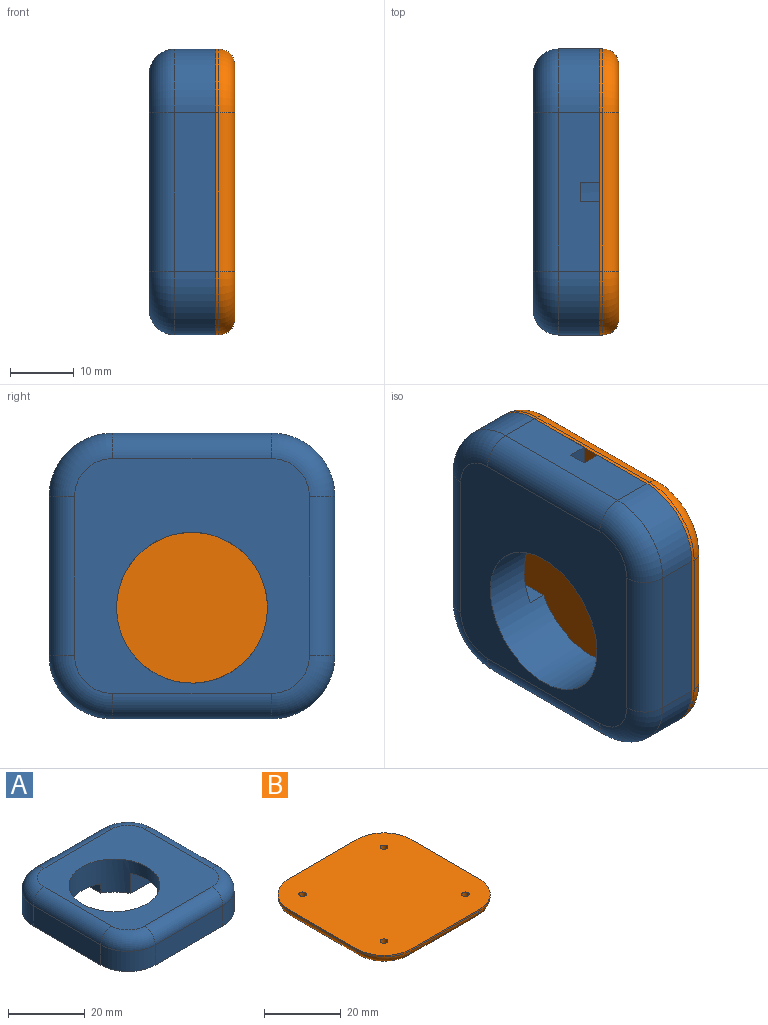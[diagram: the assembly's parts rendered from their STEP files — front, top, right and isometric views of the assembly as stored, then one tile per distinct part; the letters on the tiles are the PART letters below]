
ASSEMBLY  parts=2 mates=1
PART A: 42 faces, bbox 46.6x46.6x10.5 mm
  f0: plane 45x45mm, normal (0,0,-1), area 1167.3mm2, adj f1,f2,f3,f4,f6,f7,f8,f11
  f1: plane 25x6.5mm, normal (1,0,0), area 153.5mm2, adj f0,f7,f8,f9,f20,f21,f23
  f2: plane 25x6.5mm, normal (0,1,0), area 162.5mm2, adj f0,f18,f21,f27
  f3: plane 25x6.5mm, normal (-1,0,0), area 162.5mm2, adj f0,f18,f19,f28
  f4: plane 25x6.5mm, normal (0,-1,0), area 162.5mm2, adj f0,f19,f20,f24
  f5: plane 37x37mm, normal (0,0,1), area 895.1mm2, adj f6,f22,f23,f24,f25,f26,f27,f28
  f6: cylinder r=11.88mm len=23.75mm, axis (0,0,-1), area 647.7mm2, adj f0,f5,f10,f11,f12,f14,f15,f16
  f7: plane 3x3mm, normal (0,1,0), area 9mm2, adj f0,f1,f9,f38
  f8: plane 3x3mm, normal (0,-1,0), area 9mm2, adj f0,f1,f9,f38
  f9: plane 3x3mm, normal (0,0,-1), area 9mm2, adj f1,f7,f8,f38
  f10: plane 11x8.98mm, normal (0,0,-1), area 88.7mm2, adj f6,f11,f12,f13
  f11: plane 8.98x3mm, normal (-1,0,0), area 26.9mm2, adj f0,f6,f10,f13
  f12: plane 8.98x3mm, normal (1,0,0), area 26.9mm2, adj f0,f6,f10,f13
  f13: plane 11x3mm, normal (0,-1,0), area 33mm2, adj f0,f10,f11,f12
  f14: plane 8.98x3mm, normal (1,0,0), area 26.9mm2, adj f0,f6,f16,f17
  f15: plane 8.98x3mm, normal (-1,0,0), area 26.9mm2, adj f0,f6,f16,f17
  f16: plane 11x8.98mm, normal (0,0,-1), area 88.7mm2, adj f6,f14,f15,f17
  f17: plane 11x3mm, normal (0,1,0), area 33mm2, adj f0,f14,f15,f16
  f18: cylinder r=10mm len=10mm, axis (0,0,1), area 102.1mm2, adj f0,f2,f3,f29
  f19: cylinder r=10mm len=10mm, axis (0,0,-1), area 102.1mm2, adj f0,f3,f4,f26
  f20: cylinder r=10mm len=10mm, axis (0,0,1), area 102.1mm2, adj f0,f1,f4,f22
  f21: cylinder r=10mm len=10mm, axis (0,0,-1), area 102.1mm2, adj f0,f1,f2,f25
  f22: torus R=6mm, axis (0,0,1), area 84.4mm2, adj f5,f20,f23,f24
  f23: cylinder r=4mm len=25mm, axis (0,-1,0), area 157.1mm2, adj f1,f5,f22,f25
  f24: cylinder r=4mm len=25mm, axis (-1,0,0), area 157.1mm2, adj f4,f5,f22,f26
  f25: torus R=6mm, axis (0,0,1), area 84.4mm2, adj f5,f21,f23,f27
  f26: torus R=6mm, axis (0,0,1), area 84.4mm2, adj f5,f19,f24,f28
  f27: cylinder r=4mm len=25mm, axis (1,0,0), area 157.1mm2, adj f2,f5,f25,f29
  f28: cylinder r=4mm len=25mm, axis (0,1,0), area 157.1mm2, adj f3,f5,f26,f29
  f29: torus R=6mm, axis (0,0,1), area 84.4mm2, adj f5,f18,f27,f28
  f30: cone r=0mm half-angle=59deg, axis (0,0,-1), area 3.7mm2, adj f31
  f31: cylinder r=1mm len=8.5mm, axis (0,0,-1), area 53.4mm2, adj f0,f30
  f32: cone r=0mm half-angle=59deg, axis (0,0,-1), area 3.7mm2, adj f33
  f33: cylinder r=1mm len=8.5mm, axis (0,0,-1), area 53.4mm2, adj f0,f32
  f34: cone r=0mm half-angle=59deg, axis (0,0,-1), area 3.7mm2, adj f35
  f35: cylinder r=1mm len=8.5mm, axis (0,0,-1), area 53.4mm2, adj f0,f34
  f36: cone r=0mm half-angle=59deg, axis (0,0,-1), area 3.7mm2, adj f37
  f37: cylinder r=1mm len=8.5mm, axis (0,0,-1), area 53.4mm2, adj f0,f36
  f38: plane 10x6.5mm, normal (-1,0,0), area 56mm2, adj f0,f7,f8,f9,f39,f40,f41
  f39: plane 13.73x6.5mm, normal (0,1,0), area 89.2mm2, adj f0,f6,f38,f41
  f40: plane 13.73x6.5mm, normal (0,-1,0), area 89.2mm2, adj f0,f6,f38,f41
  f41: plane 13.73x10mm, normal (0,0,-1), area 129.9mm2, adj f6,f38,f39,f40
PART B: 26 faces, bbox 46.6x46.6x4.3 mm
  f0: plane 25x0.5mm, normal (0,1,0), area 12.5mm2, adj f4,f6,f9,f21
  f1: plane 25x0.5mm, normal (-1,0,0), area 12.5mm2, adj f4,f6,f7,f25
  f2: plane 25x0.5mm, normal (0,-1,0), area 12.5mm2, adj f4,f7,f8,f22
  f3: plane 25x0.5mm, normal (1,0,0), area 12.5mm2, adj f4,f8,f9,f18
  f4: plane 45x45mm, normal (0,0,1), area 1926.6mm2, adj f0,f1,f2,f3,f6,f7,f8,f9
  f5: plane 40x40mm, normal (0,0,-1), area 1473.2mm2, adj f11,f13,f15,f17,f18,f19,f20,f21
  f6: cylinder r=10mm len=10mm, axis (0,0,1), area 7.9mm2, adj f0,f1,f4,f23
  f7: cylinder r=10mm len=10mm, axis (0,0,-1), area 7.9mm2, adj f1,f2,f4,f24
  f8: cylinder r=10mm len=10mm, axis (0,0,1), area 7.9mm2, adj f2,f3,f4,f20
  f9: cylinder r=10mm len=10mm, axis (0,0,-1), area 7.9mm2, adj f0,f3,f4,f19
  f10: cylinder r=1mm len=2mm, axis (0,0,-1), area 9.3mm2, adj f4,f11
  f11: cone r=1mm half-angle=44.5deg, axis (0,0,-1), area 23.5mm2, adj f5,f10
  f12: cylinder r=1mm len=2mm, axis (0,0,-1), area 9.3mm2, adj f4,f13
  f13: cone r=1mm half-angle=44.5deg, axis (0,0,-1), area 23.5mm2, adj f5,f12
  f14: cylinder r=1mm len=2mm, axis (0,0,-1), area 9.3mm2, adj f4,f15
  f15: cone r=1mm half-angle=44.5deg, axis (0,0,-1), area 23.5mm2, adj f5,f14
  f16: cylinder r=1mm len=2mm, axis (0,0,-1), area 9.3mm2, adj f4,f17
  f17: cone r=1mm half-angle=44.5deg, axis (0,0,-1), area 23.5mm2, adj f5,f16
  f18: cylinder r=2.5mm len=25mm, axis (0,1,0), area 98.2mm2, adj f3,f5,f19,f20
  f19: torus R=7.5mm, axis (0,0,1), area 56.1mm2, adj f5,f9,f18,f21
  f20: torus R=7.5mm, axis (0,0,1), area 56.1mm2, adj f5,f8,f18,f22
  f21: cylinder r=2.5mm len=25mm, axis (-1,0,0), area 98.2mm2, adj f0,f5,f19,f23
  f22: cylinder r=2.5mm len=25mm, axis (1,0,0), area 98.2mm2, adj f2,f5,f20,f24
  f23: torus R=7.5mm, axis (0,0,1), area 56.1mm2, adj f5,f6,f21,f25
  f24: torus R=7.5mm, axis (0,0,1), area 56.1mm2, adj f5,f7,f22,f25
  f25: cylinder r=2.5mm len=25mm, axis (0,-1,0), area 98.2mm2, adj f1,f5,f23,f24
PLACE A rot(axis=(0,-1,0),90deg) t=(60.68,-57.81,115.95)mm
PLACE B rot(axis=(0.71,0,-0.71),180deg) t=(63.68,-57.81,125.95)mm
MATE fastened B.f16 <-> A.f32  axis (-1,0,0) through (60.68,-72.81,135.95)mm
